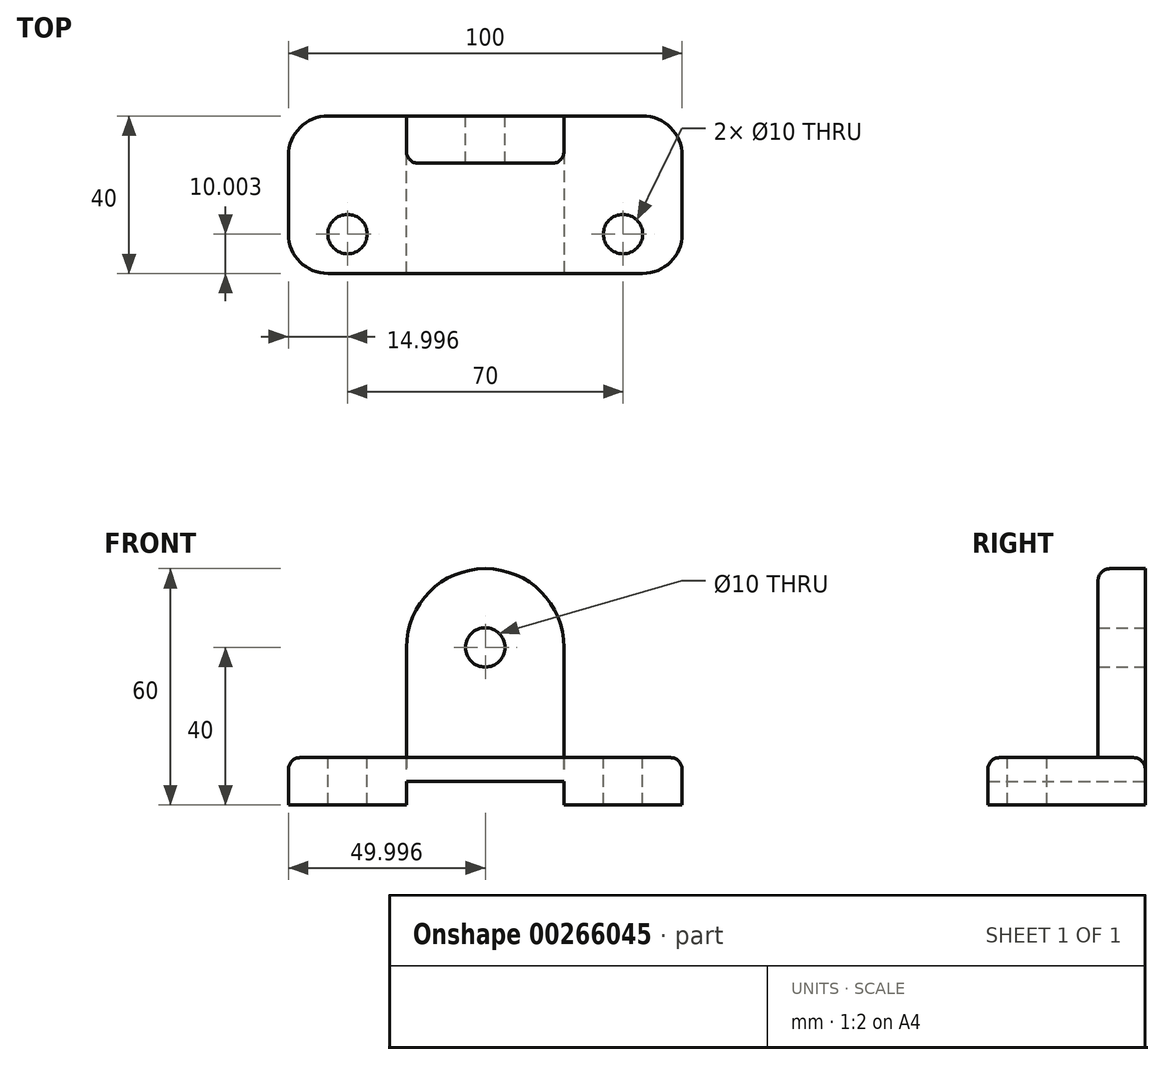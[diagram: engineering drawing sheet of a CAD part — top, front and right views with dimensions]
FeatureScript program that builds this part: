
annotation { "Feature Type Name" : "Feature", "Feature Type Description" : "" }
export const myFeature = defineFeature(function(context is Context, id is Id, definition is map)
    precondition{}
    {
        {
            var Q0;
            Q0=qCreatedBy(makeId("Top.planeOp"),FACE);
            var sketch = newSketch(context, id + "F0", { "sketchPlane" : qUnion([Q0])});
            skLineSegment(sketch, "E0", {"start": v(-42.9, 26.85) * mm, "end": v(37.1, 26.85) * mm});
            skLineSegment(sketch, "E1", {"start": v(47.1, 16.85) * mm, "end": v(47.1, -3.15) * mm});
            skLineSegment(sketch, "E2", {"start": v(37.1, -13.15) * mm, "end": v(-42.9, -13.15) * mm});
            skLineSegment(sketch, "E3", {"start": v(-52.9, -3.15) * mm, "end": v(-52.9, 16.85) * mm});
            skPoint(sketch, "E4.visualSharp", {"position": v(-52.9, -13.15) * mm});
            skArc(sketch, "E4.filletArc", {"start": v(-52.9, -3.15) * mm, "mid": v(-49.97, -10.22) * mm, "end": v(-42.9, -13.15) * mm});
            skPoint(sketch, "E5.visualSharp", {"position": v(-52.9, 26.85) * mm});
            skArc(sketch, "E5.filletArc", {"start": v(-42.9, 26.85) * mm, "mid": v(-49.97, 23.92) * mm, "end": v(-52.9, 16.85) * mm});
            skPoint(sketch, "E6.visualSharp", {"position": v(47.1, -13.15) * mm});
            skArc(sketch, "E6.filletArc", {"start": v(37.1, -13.15) * mm, "mid": v(44.18, -10.22) * mm, "end": v(47.1, -3.15) * mm});
            skPoint(sketch, "E7.visualSharp", {"position": v(47.1, 26.85) * mm});
            skArc(sketch, "E7.filletArc", {"start": v(47.1, 16.85) * mm, "mid": v(44.18, 23.92) * mm, "end": v(37.1, 26.85) * mm});
            skSolve(sketch);
        }
        {
            var Q0;
            Q0=makeQuery(id+"F0.imprint","IMPRINT",FACE,{"disambiguationData":[TD([[makeQuery(id+"F0.imprint","IMPRINT",EDGE,{"derivedFrom":sQuery(id+"F0.wireOp",EDGE,"E0")}),-1.0]])]});
            extrude(context, id + "F1", {"entities" : qUnion([Q0]), "depth" : 12 * mm});
        }
        {
            var Q0;
            Q0=makeQuery(id+"F1.opExtrude","CAP_FACE",FACE,{"disambiguationData":[OSD([sQuery(id+"F0.wireOp",EDGE,"E0"),sQuery(id+"F0.wireOp",EDGE,"E1"),sQuery(id+"F0.wireOp",EDGE,"E2"),sQuery(id+"F0.wireOp",EDGE,"E3")])],"isStart":true});
            var sketch = newSketch(context, id + "F2", { "sketchPlane" : qUnion([Q0])});
            skLineSegment(sketch, "E8", {"start": v(-22.9, 13.15) * mm, "end": v(-22.9, -26.85) * mm});
            skLineSegment(sketch, "E9", {"start": v(-22.9, -26.85) * mm, "end": v(17.1, -26.85) * mm});
            skLineSegment(sketch, "E10", {"start": v(17.1, -26.85) * mm, "end": v(17.1, 13.15) * mm});
            skLineSegment(sketch, "E11", {"start": v(17.1, 13.15) * mm, "end": v(-22.9, 13.15) * mm});
            skSolve(sketch);
        }
        {
            var Q0;
            Q0 = qSketchRegion(id + "F2", true);
            extrude(context, id + "F3", {"entities" : qUnion([Q0]), "operationType" : NewBodyOperationType.REMOVE, "oppositeDirection" : true, "depth" : 6 * mm});
        }
        {
            var Q0;
            Q0=makeQuery(id+"F1.opExtrude","CAP_FACE",FACE,{"disambiguationData":[OSD([sQuery(id+"F0.wireOp",EDGE,"E0"),sQuery(id+"F0.wireOp",EDGE,"E1"),sQuery(id+"F0.wireOp",EDGE,"E2"),sQuery(id+"F0.wireOp",EDGE,"E3")])],"isStart":false});
            var sketch = newSketch(context, id + "F4", { "sketchPlane" : qUnion([Q0])});
            skCircle(sketch, "E12", {"center": v(-37.9, -3.15) * mm, "radius": 5 * mm});
            skCircle(sketch, "E13", {"center": v(32.1, -3.15) * mm, "radius": 5 * mm});
            skSolve(sketch);
        }
        {
            var Q0;
            Q0 = qSketchRegion(id + "F4", true);
            extrude(context, id + "F5", {"entities" : qUnion([Q0]), "operationType" : NewBodyOperationType.REMOVE, "oppositeDirection" : true, "depth" : 12 * mm});
        }
        {
            var Q0;
            Q0=makeQuery(id+"F1.opExtrude","SWEPT_FACE",FACE,{"disambiguationData":[OSD([sQuery(id+"F0.wireOp",EDGE,"E0")])]});
            var sketch = newSketch(context, id + "F6", { "sketchPlane" : qUnion([Q0])});
            skLineSegment(sketch, "E14", {"start": v(-17.1, 12) * mm, "end": v(-17.1, 40) * mm});
            skLineSegment(sketch, "E15", {"start": v(22.9, 40) * mm, "end": v(22.9, 12) * mm});
            skLineSegment(sketch, "E16", {"start": v(-17.1, 12) * mm, "end": v(22.9, 12) * mm});
            skArc(sketch, "E17", {"start": v(22.9, 40) * mm, "mid": v(2.9, 60) * mm, "end": v(-17.1, 40) * mm});
            skCircle(sketch, "E18", {"center": v(2.9, 40) * mm, "radius": 5 * mm});
            skSolve(sketch);
        }
        {
            var Q0;
            Q0 = qSketchRegion(id + "F6", true);
            extrude(context, id + "F7", {"entities" : qUnion([Q0]), "operationType" : NewBodyOperationType.ADD, "oppositeDirection" : true, "depth" : 12 * mm});
        }
        {
            var Q0;
            Q0=makeQuery(id+"F1.opExtrude","CAP_EDGE",EDGE,{"disambiguationData":[OSD([sQuery(id+"F0.wireOp",EDGE,"E2")])],"isStart":false});
            var Q1;
            Q1=makeQuery(id+"F7.opExtrude","CAP_EDGE",EDGE,{"disambiguationData":[OSD([sQuery(id+"F6.wireOp",EDGE,"E16")])],"isStart":false});
            var Q2;
            Q2=makeQuery(id+"F7.opExtrude","CAP_EDGE",EDGE,{"disambiguationData":[OSD([sQuery(id+"F6.wireOp",EDGE,"E15")])],"isStart":false});
            fillet(context, id + "F8", {"entities" : qUnion([Q0, Q1, Q2]), "radius" : 3 * mm, "tangentPropagation" : true, "allowEdgeOverflow" : false});
        }
    });
